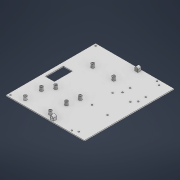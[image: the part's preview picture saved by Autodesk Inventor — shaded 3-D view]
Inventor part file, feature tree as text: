
AUTODESK INVENTOR PART (.ipt)
format: ipt  version: 2021 (Build 250183000, 183)  size: 467,968 bytes
history: native  units: mm
features: extrude x12, sketch x11, projected_geometry x7, other x1, fillet x1
ambient origin geometry x8: Origin, YZ Plane, XZ Plane, XY Plane, X Axis, Y Axis, Z Axis, Center Point
bodies: Volumenkörper1 (feature_tree)
feature tree (32):
  other  "Obenplatte_vorne"
  extrude  "Extrusion1"  Depth=200.0mm
  extrude  "Extrusion2"  Depth=2.0mm
  extrude  "Extrusion3"  Depth=42.0mm
  extrude  "Extrusion4"  Depth=5.0mm
  extrude  "Extrusion5"  TaperAngle=0.0deg  [1 undecoded]
  extrude  "Extrusion6"  Depth=10.5mm
  extrude  "Extrusion7"  Depth=3.2mm
  extrude  "Extrusion8"  Depth=23.0mm
  extrude  "Extrusion9"  Depth=23.0mm
  fillet  "Rundung1"  Radius=74.5mm
  extrude  "Extrusion10"  Depth=23.0mm
  extrude  "Extrusion11"  Depth=6.0mm
  extrude  "Extrusion12"  Depth=6.0mm
  sketch  "Skizze1"  dims[d0=175.0mm d1=200.0mm]
  sketch  "Skizze2"  dims[d2=2.0mm d3=0.0mm d4=3.2mm]
  sketch  "Skizze3"  dims[d5=3.2mm d6=42.0mm]
  sketch  "Skizze5"  dims[d7=5.0mm d9=5.0mm]
  projected_geometry  "Projizierte Kontur1"
  projected_geometry  "Projizierte Kontur2"
  projected_geometry  "Projizierte Kontur3"
  projected_geometry  "Projizierte Kontur4"
  sketch  "Skizze6"  dims[d10=42.0mm d11=0.0mm]
  sketch  "Skizze7"  dims[d35=3.2mm d36=10.5mm]
  sketch  "Skizze8"  dims[d37=23.0mm d38=3.2mm]
  sketch  "Skizze9"  dims[d39=74.5mm d40=23.0mm]
  sketch  "Skizze10"  dims[d41=3.2mm d42=23.0mm d43=74.5mm]
  sketch  "Skizze11"  dims[d44=3.2mm d45=23.0mm]
  sketch  "Skizze12"  dims[d46=10.5mm d47=3.2mm d48=60.0mm d49=77.0mm d50=3.2mm d51=60.0mm d52=77.0mm d53=60.0mm d54=0.0mm d55=5.0mm d56=33.0mm d57=53.34mm d58=101.6mm d59=40.0mm d60=7.0mm d61=86.36mm d62=50.8mm d63=7.0mm d64=90.17mm d65=50.8mm d66=7.0mm d67=96.52mm d68=50.8mm d69=7.0mm d70=87.63mm d71=50.8mm d72=7.0mm d73=0.0mm d74=4.0mm d75=4.0mm d76=4.0mm d77=4.0mm d78=5.0mm d79=0.0mm d80=3.2mm d81=3.2mm d82=15.0mm d83=15.0mm d84=35.0mm d85=17.0mm d86=5.0mm d87=0.0mm d88=3.2mm d89=3.2mm d90=50.0mm d91=50.0mm d92=35.0mm d94=17.0mm d95=103.5mm d96=7.0mm d97=7.0mm d98=2.2mm d99=9.0mm d100=0.0mm d101=4.0mm d102=5.0mm d103=3.5mm d104=5.0mm d105=0.0mm d107=4.0mm d108=3.5mm d109=5.0mm d110=5.0mm d111=0.0mm d112=3.5mm d113=20.0mm d114=40.0mm d115=8.0mm d116=10.0mm d117=0.0mm d118=7.0mm d119=7.0mm d120=7.0mm d121=7.0mm d122=30.0mm d123=30.0mm d126=56.0mm d127=36.0mm d128=56.0mm d129=36.0mm d130=7.0mm d131=0.0mm d132=4.3mm d133=4.3mm d134=4.3mm d135=4.3mm d136=6.0mm d137=0.0mm d138=13.0mm d139=13.0mm d140=35.0mm]
  projected_geometry  "Projizierte Kontur5"
  projected_geometry  "Projizierte Kontur6"
  projected_geometry  "Projizierte Kontur7"
note: 1 required parameter value undecoded (feature->parameter linkage not recoverable at this tier; creation-order binding heuristic only, values carry confidence <= 0.55)
